# Revit family: KINGSLEY Hand Shower Holder and BP – BRUSHED BRASS (SKU 12651)
name_source: partatom
category: Generic Models
units: mm (PartAtom-declared; Revit-internal decimal feet)

## family parameters
Always vertical = Yes
Can host rebar = No
Cut with Voids When Loaded = No
Maintain Annotation Orientation = No
Part Type = Normal
Room Calculation Point = No
Round Connector Dimension = Use Diameter
Shared = No
Work Plane-Based = No

## types (1)
- KINGSLEY HAND SHOWER HOLDER AND BP – BRUSHED BRASS (SKU 12651)
    Default Elevation = 0 mm  [stored 0 ft]
    Description = KINGSLEY Hand Shower Holder And BP – BRUSHED BRASS (SKU 12651)
    Manufacturer = ABI Interiors PTY LTD
    Model = BRUSHED BRASS (SKU 12651)
    URL = https://www.abiinteriors.com.au

note: [stored X ft] marks values corroborated as IEEE doubles in the binary element streams (Revit-internal decimal feet)

## geometry (parser evidence)
native form markers: Sweep x3
no freeform markers — native parametric forms only
